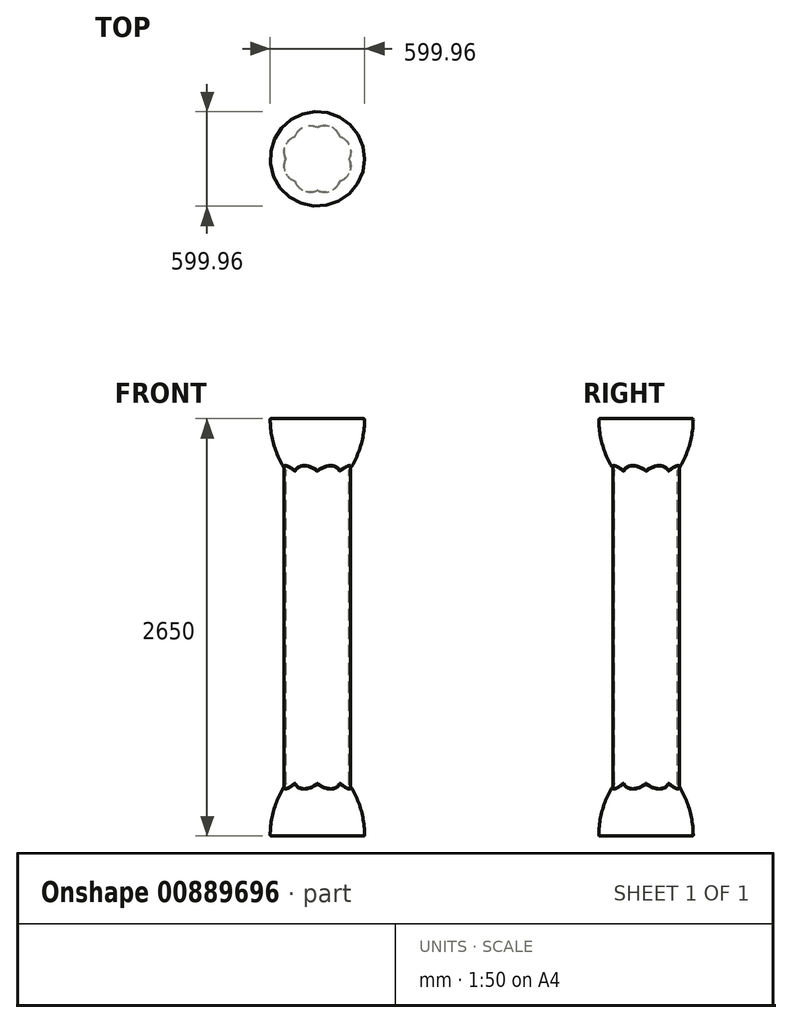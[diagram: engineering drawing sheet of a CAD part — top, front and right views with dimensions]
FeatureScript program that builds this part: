
annotation { "Feature Type Name" : "Feature", "Feature Type Description" : "" }
export const myFeature = defineFeature(function(context is Context, id is Id, definition is map)
    precondition{}
    {
        {
            var Q0;
            Q0=qCreatedBy(makeId("Top.planeOp"),FACE);
            var sketch = newSketch(context, id + "F0", { "sketchPlane" : qUnion([Q0])});
            skCircle(sketch, "E0.cCircle", {"center": v(0, 0) * mm, "radius": 200 * mm, "construction": true});
            skLineSegment(sketch, "E0.0", {"start": v(141.42, 141.42) * mm, "end": v(200, 0) * mm});
            skLineSegment(sketch, "E0.1", {"start": v(200, 0) * mm, "end": v(141.42, -141.42) * mm});
            skLineSegment(sketch, "E0.2", {"start": v(141.42, -141.42) * mm, "end": v(0, -200) * mm});
            skLineSegment(sketch, "E0.3", {"start": v(0, -200) * mm, "end": v(-141.42, -141.42) * mm});
            skLineSegment(sketch, "E0.4", {"start": v(-141.42, -141.42) * mm, "end": v(-200, 0) * mm});
            skLineSegment(sketch, "E0.5", {"start": v(-200, 0) * mm, "end": v(-141.42, 141.42) * mm});
            skLineSegment(sketch, "E0.6", {"start": v(-141.42, 141.42) * mm, "end": v(0, 200) * mm});
            skLineSegment(sketch, "E0.7", {"start": v(0, 200) * mm, "end": v(141.42, 141.42) * mm});
            skLineSegment(sketch, "E1", {"start": v(0, 0) * mm, "end": v(0, 200) * mm});
            skArc(sketch, "E2", {"start": v(0, 200) * mm, "mid": v(-84.35, 203.64) * mm, "end": v(-141.42, 141.42) * mm});
            skArc(sketch, "E3", {"start": v(-141.42, 141.42) * mm, "mid": v(-203.64, 84.35) * mm, "end": v(-200, 0) * mm});
            skArc(sketch, "E4", {"start": v(-200, 0) * mm, "mid": v(-203.64, -84.35) * mm, "end": v(-141.42, -141.42) * mm});
            skArc(sketch, "E5", {"start": v(-141.42, -141.42) * mm, "mid": v(-84.35, -203.64) * mm, "end": v(0, -200) * mm});
            skArc(sketch, "E6", {"start": v(0, -200) * mm, "mid": v(84.35, -203.64) * mm, "end": v(141.42, -141.42) * mm});
            skArc(sketch, "E7", {"start": v(141.42, -141.42) * mm, "mid": v(203.64, -84.35) * mm, "end": v(200, 0) * mm});
            skArc(sketch, "E8", {"start": v(200, 0) * mm, "mid": v(203.64, 84.35) * mm, "end": v(141.42, 141.42) * mm});
            skArc(sketch, "E9", {"start": v(141.42, 141.42) * mm, "mid": v(84.35, 203.64) * mm, "end": v(0, 200) * mm});
            skSolve(sketch);
        }
        {
            var Q0;
            Q0 = qSketchRegion(id + "F0", true);
            extrude(context, id + "F1", {"entities" : qUnion([Q0]), "depth" : 2650 * mm, "offsetDistance" : 25 * mm});
        }
        {
            var Q0;
            Q0=qCreatedBy(makeId("Right.planeOp"),FACE);
            var sketch = newSketch(context, id + "F2", { "sketchPlane" : qUnion([Q0])});
            skLineSegment(sketch, "E10", {"start": v(0, 0) * mm, "end": v(-300, 0) * mm});
            skArc(sketch, "E11", {"start": v(300, 0) * mm, "mid": v(219.62, 300) * mm, "end": v(0, 519.62) * mm});
            skLineSegment(sketch, "E12", {"start": v(0, 0) * mm, "end": v(300, 0) * mm});
            skLineSegment(sketch, "E13", {"start": v(0, 0) * mm, "end": v(0, 2650) * mm});
            skLineSegment(sketch, "E14", {"start": v(0, 2650) * mm, "end": v(-300, 2650) * mm});
            skArc(sketch, "E15", {"start": v(0, 2130.38) * mm, "mid": v(219.62, 2350) * mm, "end": v(300, 2650) * mm});
            skLineSegment(sketch, "E16", {"start": v(0, 2650) * mm, "end": v(300, 2650) * mm});
            skLineSegment(sketch, "E17", {"start": v(0, 2650) * mm, "end": v(0, 2130.38) * mm});
            skLineSegment(sketch, "E18", {"start": v(0, 0) * mm, "end": v(0, 519.62) * mm});
            skSolve(sketch);
        }
        {
            var Q0;
            Q0=makeQuery(id+"F2.imprint","IMPRINT",FACE,{"disambiguationData":[TD([[makeQuery(id+"F2.imprint","IMPRINT",EDGE,{"derivedFrom":sQuery(id+"F2.wireOp",EDGE,"E11")}),1.0]])]});
            var Q1;
            Q1=makeQuery(id+"F2.imprint","IMPRINT",FACE,{"disambiguationData":[TD([[makeQuery(id+"F2.imprint","IMPRINT",EDGE,{"derivedFrom":sQuery(id+"F2.wireOp",EDGE,"E15")}),1.0]])]});
            var Q2;
            Q2=sQuery(id+"F2.wireOp",EDGE,"E11");
            var Q3;
            Q3=sQuery(id+"F2.wireOp",EDGE,"E12");
            var Q4;
            Q4=sQuery(id+"F2.wireOp",EDGE,"E13");
            revolve(context, id + "F3", {"operationType" : NewBodyOperationType.ADD, "surfaceOperationType" : NewSurfaceOperationType.NEW, "entities" : qUnion([Q0, Q1]), "surfaceEntities" : qUnion([Q2, Q3]), "axis" : qUnion([Q4]), "revolveType" : RevolveType.FULL});
        }
        {
            var Q0;
            Q0=makeQuery(id+"F3.opRevolve","SWEPT_EDGE",EDGE,{"disambiguationData":[OSD([sQuery(id+"F2.wireOp",EDGE,"E11"),sQuery(id+"F2.wireOp",EDGE,"E12")])]});
            var Q1;
            Q1=makeQuery(id+"F3.boolean.opBoolean","INTERSECT",EDGE,{"derivedFrom":[makeQuery(id+"F1.opExtrude","SWEPT_FACE",FACE,{"disambiguationData":[OSD([sQuery(id+"F0.wireOp",EDGE,"E9")])]}),makeQuery(id+"F3.opRevolve","SWEPT_FACE",FACE,{"disambiguationData":[OSD([sQuery(id+"F2.wireOp",EDGE,"E15")])]})]});
            var Q2;
            Q2=makeQuery(id+"F3.opRevolve","SWEPT_EDGE",EDGE,{"disambiguationData":[OSD([sQuery(id+"F2.wireOp",EDGE,"E15"),sQuery(id+"F2.wireOp",EDGE,"E16")])]});
            var Q3;
            Q3=makeQuery(id+"F3.boolean.opBoolean","INTERSECT",EDGE,{"derivedFrom":[makeQuery(id+"F1.opExtrude","SWEPT_FACE",FACE,{"disambiguationData":[OSD([sQuery(id+"F0.wireOp",EDGE,"E2")])]}),makeQuery(id+"F3.opRevolve","SWEPT_FACE",FACE,{"disambiguationData":[OSD([sQuery(id+"F2.wireOp",EDGE,"E11")])]})]});
            var Q4;
            Q4=makeQuery(id+"F3.boolean.opBoolean","INTERSECT",EDGE,{"derivedFrom":[makeQuery(id+"F1.opExtrude","SWEPT_FACE",FACE,{"disambiguationData":[OSD([sQuery(id+"F0.wireOp",EDGE,"E8")])]}),makeQuery(id+"F3.opRevolve","SWEPT_FACE",FACE,{"disambiguationData":[OSD([sQuery(id+"F2.wireOp",EDGE,"E11")])]})]});
            var Q5;
            Q5=makeQuery(id+"F3.boolean.opBoolean","INTERSECT",EDGE,{"derivedFrom":[makeQuery(id+"F1.opExtrude","SWEPT_FACE",FACE,{"disambiguationData":[OSD([sQuery(id+"F0.wireOp",EDGE,"E2")])]}),makeQuery(id+"F3.opRevolve","SWEPT_FACE",FACE,{"disambiguationData":[OSD([sQuery(id+"F2.wireOp",EDGE,"E15")])]})]});
            var Q6;
            Q6=makeQuery(id+"F3.boolean.opBoolean","INTERSECT",EDGE,{"derivedFrom":[makeQuery(id+"F1.opExtrude","SWEPT_FACE",FACE,{"disambiguationData":[OSD([sQuery(id+"F0.wireOp",EDGE,"E8")])]}),makeQuery(id+"F3.opRevolve","SWEPT_FACE",FACE,{"disambiguationData":[OSD([sQuery(id+"F2.wireOp",EDGE,"E15")])]})]});
            var Q7;
            Q7=makeQuery(id+"F3.boolean.opBoolean","INTERSECT",EDGE,{"derivedFrom":[makeQuery(id+"F1.opExtrude","SWEPT_FACE",FACE,{"disambiguationData":[OSD([sQuery(id+"F0.wireOp",EDGE,"E9")])]}),makeQuery(id+"F3.opRevolve","SWEPT_FACE",FACE,{"disambiguationData":[OSD([sQuery(id+"F2.wireOp",EDGE,"E11")])]})]});
            var Q8;
            Q8=makeQuery(id+"F3.boolean.opBoolean","INTERSECT",EDGE,{"derivedFrom":[makeQuery(id+"F1.opExtrude","SWEPT_FACE",FACE,{"disambiguationData":[OSD([sQuery(id+"F0.wireOp",EDGE,"E7")])]}),makeQuery(id+"F3.opRevolve","SWEPT_FACE",FACE,{"disambiguationData":[OSD([sQuery(id+"F2.wireOp",EDGE,"E15")])]})]});
            var Q9;
            Q9=makeQuery(id+"F3.boolean.opBoolean","INTERSECT",EDGE,{"derivedFrom":[makeQuery(id+"F1.opExtrude","SWEPT_FACE",FACE,{"disambiguationData":[OSD([sQuery(id+"F0.wireOp",EDGE,"E7")])]}),makeQuery(id+"F3.opRevolve","SWEPT_FACE",FACE,{"disambiguationData":[OSD([sQuery(id+"F2.wireOp",EDGE,"E11")])]})]});
            var Q10;
            Q10=makeQuery(id+"F1.opExtrude","SWEPT_EDGE",EDGE,{"disambiguationData":[OSD([sQuery(id+"F0.wireOp",EDGE,"E0.0"),sQuery(id+"F0.wireOp",EDGE,"E0.7"),sQuery(id+"F0.wireOp",EDGE,"E8"),sQuery(id+"F0.wireOp",EDGE,"E9")])]});
            var Q11;
            Q11=makeQuery(id+"F3.boolean.opBoolean","INTERSECT",EDGE,{"derivedFrom":[makeQuery(id+"F1.opExtrude","SWEPT_FACE",FACE,{"disambiguationData":[OSD([sQuery(id+"F0.wireOp",EDGE,"E3")])]}),makeQuery(id+"F3.opRevolve","SWEPT_FACE",FACE,{"disambiguationData":[OSD([sQuery(id+"F2.wireOp",EDGE,"E11")])]})]});
            var Q12;
            Q12=makeQuery(id+"F1.opExtrude","SWEPT_EDGE",EDGE,{"disambiguationData":[OSD([sQuery(id+"F0.wireOp",EDGE,"E0.5"),sQuery(id+"F0.wireOp",EDGE,"E0.6"),sQuery(id+"F0.wireOp",EDGE,"E2"),sQuery(id+"F0.wireOp",EDGE,"E3")])]});
            var Q13;
            Q13=makeQuery(id+"F1.opExtrude","SWEPT_EDGE",EDGE,{"disambiguationData":[OSD([sQuery(id+"F0.wireOp",EDGE,"E0.6"),sQuery(id+"F0.wireOp",EDGE,"E0.7"),sQuery(id+"F0.wireOp",EDGE,"E2"),sQuery(id+"F0.wireOp",EDGE,"E9")])]});
            var Q14;
            Q14=makeQuery(id+"F3.boolean.opBoolean","INTERSECT",EDGE,{"derivedFrom":[makeQuery(id+"F1.opExtrude","SWEPT_FACE",FACE,{"disambiguationData":[OSD([sQuery(id+"F0.wireOp",EDGE,"E5")])]}),makeQuery(id+"F3.opRevolve","SWEPT_FACE",FACE,{"disambiguationData":[OSD([sQuery(id+"F2.wireOp",EDGE,"E15")])]})]});
            var Q15;
            Q15=makeQuery(id+"F3.boolean.opBoolean","INTERSECT",EDGE,{"derivedFrom":[makeQuery(id+"F1.opExtrude","SWEPT_FACE",FACE,{"disambiguationData":[OSD([sQuery(id+"F0.wireOp",EDGE,"E4")])]}),makeQuery(id+"F3.opRevolve","SWEPT_FACE",FACE,{"disambiguationData":[OSD([sQuery(id+"F2.wireOp",EDGE,"E15")])]})]});
            var Q16;
            Q16=makeQuery(id+"F3.boolean.opBoolean","INTERSECT",EDGE,{"derivedFrom":[makeQuery(id+"F1.opExtrude","SWEPT_FACE",FACE,{"disambiguationData":[OSD([sQuery(id+"F0.wireOp",EDGE,"E6")])]}),makeQuery(id+"F3.opRevolve","SWEPT_FACE",FACE,{"disambiguationData":[OSD([sQuery(id+"F2.wireOp",EDGE,"E15")])]})]});
            var Q17;
            Q17=makeQuery(id+"F3.boolean.opBoolean","INTERSECT",EDGE,{"derivedFrom":[makeQuery(id+"F1.opExtrude","SWEPT_FACE",FACE,{"disambiguationData":[OSD([sQuery(id+"F0.wireOp",EDGE,"E3")])]}),makeQuery(id+"F3.opRevolve","SWEPT_FACE",FACE,{"disambiguationData":[OSD([sQuery(id+"F2.wireOp",EDGE,"E15")])]})]});
            var Q18;
            Q18=makeQuery(id+"F3.boolean.opBoolean","INTERSECT",EDGE,{"derivedFrom":[makeQuery(id+"F1.opExtrude","SWEPT_FACE",FACE,{"disambiguationData":[OSD([sQuery(id+"F0.wireOp",EDGE,"E5")])]}),makeQuery(id+"F3.opRevolve","SWEPT_FACE",FACE,{"disambiguationData":[OSD([sQuery(id+"F2.wireOp",EDGE,"E11")])]})]});
            var Q19;
            Q19=makeQuery(id+"F1.opExtrude","SWEPT_EDGE",EDGE,{"disambiguationData":[OSD([sQuery(id+"F0.wireOp",EDGE,"E0.0"),sQuery(id+"F0.wireOp",EDGE,"E0.1"),sQuery(id+"F0.wireOp",EDGE,"E7"),sQuery(id+"F0.wireOp",EDGE,"E8")])]});
            var Q20;
            Q20=makeQuery(id+"F3.boolean.opBoolean","INTERSECT",EDGE,{"derivedFrom":[makeQuery(id+"F1.opExtrude","SWEPT_FACE",FACE,{"disambiguationData":[OSD([sQuery(id+"F0.wireOp",EDGE,"E6")])]}),makeQuery(id+"F3.opRevolve","SWEPT_FACE",FACE,{"disambiguationData":[OSD([sQuery(id+"F2.wireOp",EDGE,"E11")])]})]});
            var Q21;
            Q21=makeQuery(id+"F1.opExtrude","SWEPT_EDGE",EDGE,{"disambiguationData":[OSD([sQuery(id+"F0.wireOp",EDGE,"E0.4"),sQuery(id+"F0.wireOp",EDGE,"E0.5"),sQuery(id+"F0.wireOp",EDGE,"E3"),sQuery(id+"F0.wireOp",EDGE,"E4")])]});
            var Q22;
            Q22=makeQuery(id+"F3.boolean.opBoolean","INTERSECT",EDGE,{"derivedFrom":[makeQuery(id+"F1.opExtrude","SWEPT_FACE",FACE,{"disambiguationData":[OSD([sQuery(id+"F0.wireOp",EDGE,"E4")])]}),makeQuery(id+"F3.opRevolve","SWEPT_FACE",FACE,{"disambiguationData":[OSD([sQuery(id+"F2.wireOp",EDGE,"E11")])]})]});
            var Q23;
            Q23=makeQuery(id+"F1.opExtrude","SWEPT_EDGE",EDGE,{"disambiguationData":[OSD([sQuery(id+"F0.wireOp",EDGE,"E0.2"),sQuery(id+"F0.wireOp",EDGE,"E0.3"),sQuery(id+"F0.wireOp",EDGE,"E5"),sQuery(id+"F0.wireOp",EDGE,"E6")])]});
            var Q24;
            Q24=makeQuery(id+"F1.opExtrude","SWEPT_EDGE",EDGE,{"disambiguationData":[OSD([sQuery(id+"F0.wireOp",EDGE,"E0.3"),sQuery(id+"F0.wireOp",EDGE,"E0.4"),sQuery(id+"F0.wireOp",EDGE,"E4"),sQuery(id+"F0.wireOp",EDGE,"E5")])]});
            var Q25;
            Q25=makeQuery(id+"F1.opExtrude","SWEPT_EDGE",EDGE,{"disambiguationData":[OSD([sQuery(id+"F0.wireOp",EDGE,"E0.1"),sQuery(id+"F0.wireOp",EDGE,"E0.2"),sQuery(id+"F0.wireOp",EDGE,"E6"),sQuery(id+"F0.wireOp",EDGE,"E7")])]});
            fillet(context, id + "F4", {"entities" : qUnion([Q0, Q1, Q2, Q3, Q4, Q5, Q6, Q7, Q8, Q9, Q10, Q11, Q12, Q13, Q14, Q15, Q16, Q17, Q18, Q19, Q20, Q21, Q22, Q23, Q24, Q25]), "radius" : 5 * mm, "tangentPropagation" : true, "allowEdgeOverflow" : false});
        }
    });
